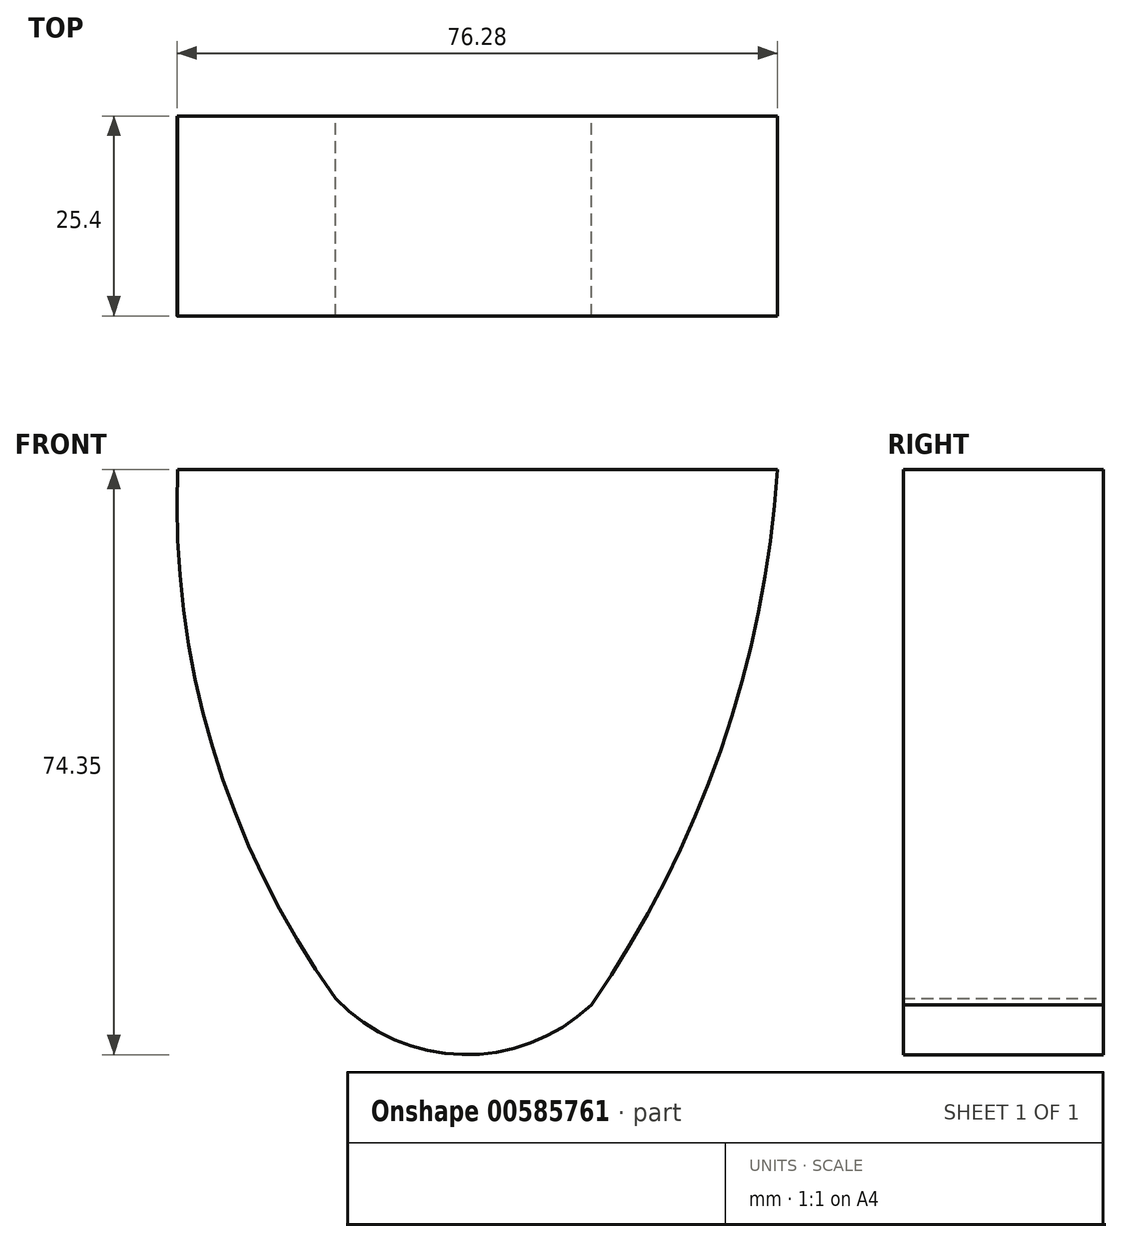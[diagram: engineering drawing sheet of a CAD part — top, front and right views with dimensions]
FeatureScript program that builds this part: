
annotation { "Feature Type Name" : "Feature", "Feature Type Description" : "" }
export const myFeature = defineFeature(function(context is Context, id is Id, definition is map)
    precondition{}
    {
        {
            var Q0;
            Q0=qCreatedBy(makeId("Front.planeOp"),FACE);
            var sketch = newSketch(context, id + "F0", { "sketchPlane" : qUnion([Q0])});
            skLineSegment(sketch, "E0", {"start": v(0, 0) * mm, "end": v(76.2, 0) * mm});
            skArc(sketch, "E1", {"start": v(52.56, -68.04) * mm, "mid": v(36.16, -74.34) * mm, "end": v(20.1, -67.22) * mm});
            skArc(sketch, "E2", {"start": v(52.56, -68.04) * mm, "mid": v(69, -35.63) * mm, "end": v(76.2, 0) * mm});
            skArc(sketch, "E3", {"start": v(0, 0) * mm, "mid": v(4.45, -35.28) * mm, "end": v(20.1, -67.22) * mm});
            skSolve(sketch);
        }
        {
            var Q0;
            Q0=makeQuery(id+"F0.imprint","IMPRINT",FACE,{"disambiguationData":[TD([[makeQuery(id+"F0.imprint","IMPRINT",EDGE,{"derivedFrom":sQuery(id+"F0.wireOp",EDGE,"E0")}),-1.0]])]});
            extrude(context, id + "F1", {"entities" : qUnion([Q0]), "depth" : 25.4 * mm, "offsetDistance" : 25.4 * mm});
        }
    });
